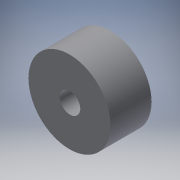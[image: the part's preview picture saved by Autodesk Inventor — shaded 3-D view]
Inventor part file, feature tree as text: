
AUTODESK INVENTOR PART (.ipt)
format: ipt  version: 2019 (Build 230136000, 136)  size: 99,840 bytes
history: native  units: in
note: dims shown in document units (in); Inventor stores cm internally (conversion verified against a paired STEP export)
features: sketch x2, extrude x1, hole x1
ambient origin geometry x8: Origin, YZ Plane, XZ Plane, XY Plane, X Axis, Y Axis, Z Axis, Center Point
bodies: Solid1 (feature_tree)
feature tree (4):
  extrude  "Extrusion1"  Depth=0.7874in TaperAngle=0.0deg
  hole  "Hole1"  [1 undecoded]
  sketch  "Sketch1"  dims[d0=1.5748in d1=0.7874in d2=0.0in]
  sketch  "Sketch2"  dims[d3=0.3937in d4=0.75in d5=0.375in d6=0.25in d7=0.5635in d8=1.1811in d9=0.8108in]
note: 1 required parameter value undecoded (feature->parameter linkage not recoverable at this tier; creation-order binding heuristic only, values carry confidence <= 0.55)
